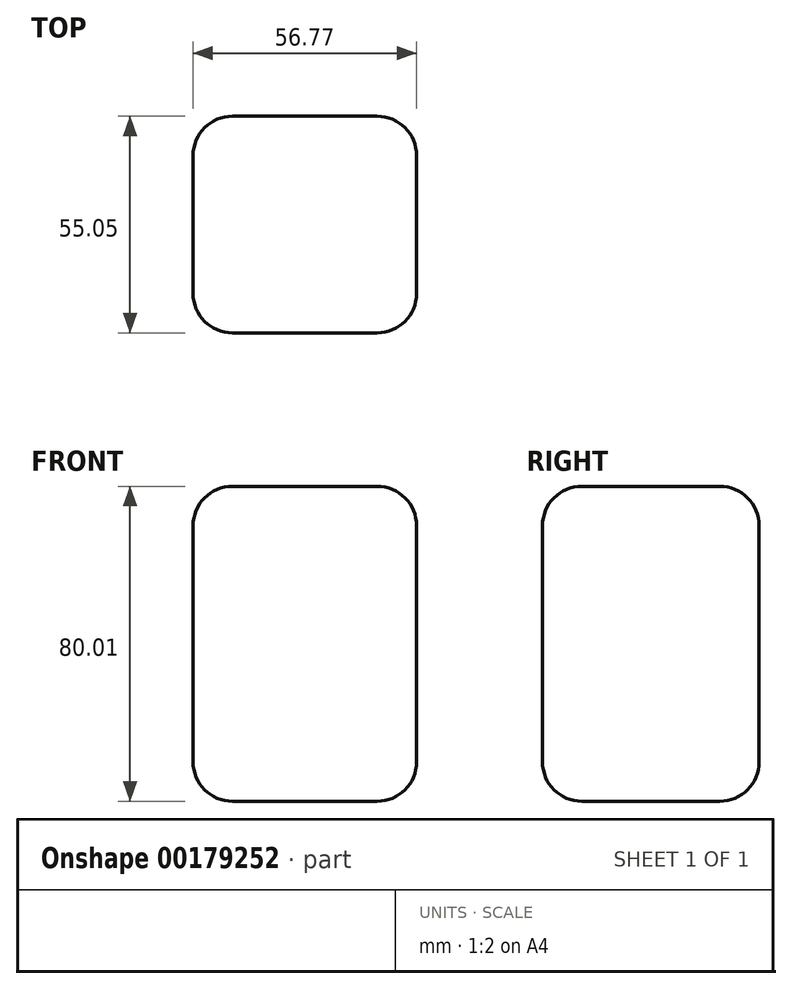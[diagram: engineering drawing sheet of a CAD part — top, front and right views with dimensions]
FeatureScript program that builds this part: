
annotation { "Feature Type Name" : "Feature", "Feature Type Description" : "" }
export const myFeature = defineFeature(function(context is Context, id is Id, definition is map)
    precondition{}
    {
        {
            var Q0;
            Q0=qCreatedBy(makeId("Top.planeOp"),FACE);
            var sketch = newSketch(context, id + "F0", { "sketchPlane" : qUnion([Q0])});
            skLineSegment(sketch, "E0.bottom", {"start": v(-30.53, 29.52) * mm, "end": v(26.24, 29.52) * mm});
            skLineSegment(sketch, "E0.top", {"start": v(-30.53, -25.53) * mm, "end": v(26.24, -25.53) * mm});
            skLineSegment(sketch, "E0.left", {"start": v(-30.53, 29.52) * mm, "end": v(-30.53, -25.53) * mm});
            skLineSegment(sketch, "E0.right", {"start": v(26.24, 29.52) * mm, "end": v(26.24, -25.53) * mm});
            skSolve(sketch);
        }
        {
            var Q0;
            Q0 = qSketchRegion(id + "F0", true);
            extrude(context, id + "F1", {"entities" : qUnion([Q0]), "depth" : 80 * mm});
        }
        {
            var Q0;
            Q0=makeQuery(id+"F1.opExtrude","SWEPT_FACE",FACE,{"disambiguationData":[OSD([sQuery(id+"F0.wireOp",EDGE,"E0.left")])]});
            var Q1;
            Q1=makeQuery(id+"F1.opExtrude","SWEPT_FACE",FACE,{"disambiguationData":[OSD([sQuery(id+"F0.wireOp",EDGE,"E0.top")])]});
            var Q2;
            Q2=makeQuery(id+"F1.opExtrude","CAP_FACE",FACE,{"disambiguationData":[OSD([sQuery(id+"F0.wireOp",EDGE,"E0.bottom"),sQuery(id+"F0.wireOp",EDGE,"E0.top"),sQuery(id+"F0.wireOp",EDGE,"E0.left"),sQuery(id+"F0.wireOp",EDGE,"E0.right")])],"isStart":false});
            var Q3;
            Q3=makeQuery(id+"F1.opExtrude","SWEPT_FACE",FACE,{"disambiguationData":[OSD([sQuery(id+"F0.wireOp",EDGE,"E0.bottom")])]});
            var Q4;
            Q4=makeQuery(id+"F1.opExtrude","SWEPT_FACE",FACE,{"disambiguationData":[OSD([sQuery(id+"F0.wireOp",EDGE,"E0.right")])]});
            fillet(context, id + "F2", {"entities" : qUnion([Q0, Q1, Q2, Q3, Q4]), "radius" : 10 * mm, "tangentPropagation" : true, "allowEdgeOverflow" : false});
        }
    });
